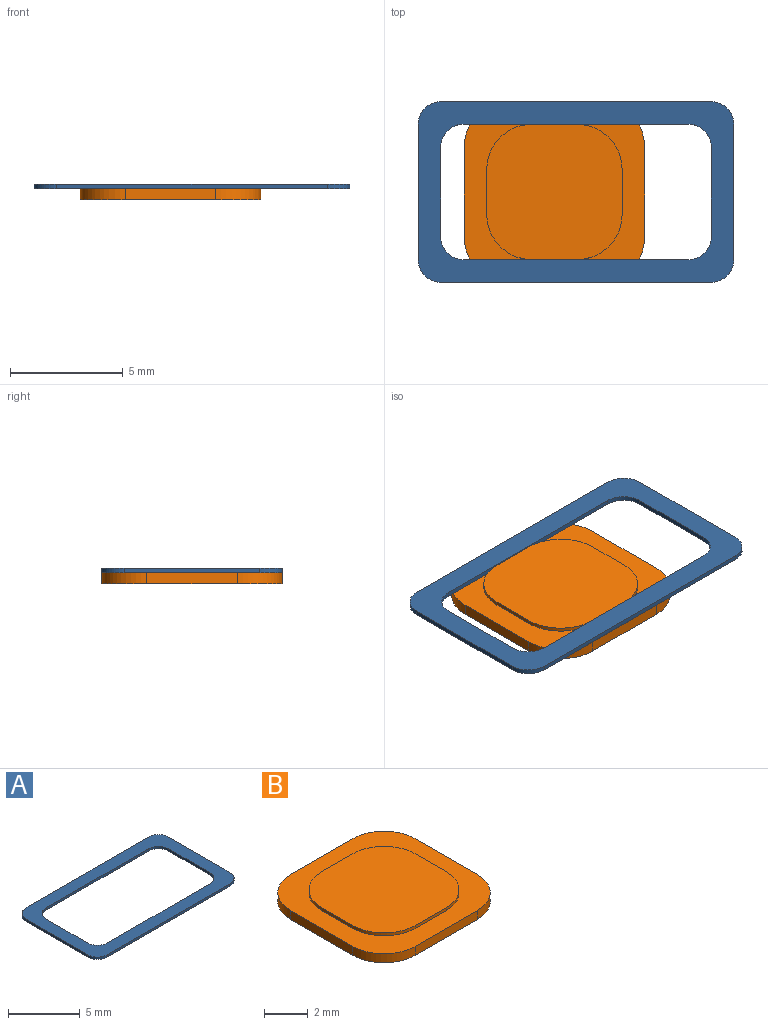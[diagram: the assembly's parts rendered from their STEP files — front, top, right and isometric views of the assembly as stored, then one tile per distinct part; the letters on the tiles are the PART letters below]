
ASSEMBLY  parts=2 mates=1
PART A: 18 faces, bbox 14x8x0.2 mm
  f0: plane 14x8mm, normal (0,0,1), area 40mm2, adj f2,f3,f4,f5,f6,f7,f8,f9
  f1: plane 14x8mm, normal (0,0,-1), area 40mm2, adj f2,f3,f4,f5,f6,f7,f8,f9
  f2: plane 12x0.2mm, normal (0,-1,0), area 2.4mm2, adj f0,f1,f3,f9
  f3: cylinder r=1mm len=1mm, axis (0,0,-1), area 0.3mm2, adj f0,f1,f2,f4
  f4: plane 6x0.2mm, normal (1,0,0), area 1.2mm2, adj f0,f1,f3,f5
  f5: cylinder r=1mm len=1mm, axis (0,0,-1), area 0.3mm2, adj f0,f1,f4,f6
  f6: plane 12x0.2mm, normal (0,1,0), area 2.4mm2, adj f0,f1,f5,f7
  f7: cylinder r=1mm len=1mm, axis (0,0,-1), area 0.3mm2, adj f0,f1,f6,f8
  f8: plane 6x0.2mm, normal (-1,0,0), area 1.2mm2, adj f0,f1,f7,f9
  f9: cylinder r=1mm len=1mm, axis (0,0,-1), area 0.3mm2, adj f0,f1,f2,f8
  f10: cylinder r=1mm len=1mm, axis (0,0,-1), area 0.3mm2, adj f0,f1,f11,f17
  f11: plane 10x0.2mm, normal (0,1,0), area 2mm2, adj f0,f1,f10,f12
  f12: cylinder r=1mm len=1mm, axis (0,0,-1), area 0.3mm2, adj f0,f1,f11,f13
  f13: plane 4x0.2mm, normal (-1,0,0), area 0.8mm2, adj f0,f1,f12,f14
  f14: cylinder r=1mm len=1mm, axis (0,0,-1), area 0.3mm2, adj f0,f1,f13,f15
  f15: plane 10x0.2mm, normal (0,-1,0), area 2mm2, adj f0,f1,f14,f16
  f16: cylinder r=1mm len=1mm, axis (0,0,-1), area 0.3mm2, adj f0,f1,f15,f17
  f17: plane 4x0.2mm, normal (1,0,0), area 0.8mm2, adj f0,f1,f10,f16
PART B: 19 faces, bbox 8x8x0.7 mm
  f0: plane 8x8mm, normal (0,0,1), area 28mm2, adj f1,f2,f3,f4,f5,f6,f7,f8
  f1: cylinder r=2mm len=2mm, axis (0,0,1), area 1.6mm2, adj f0,f2,f8,f9
  f2: plane 4x0.5mm, normal (0,-1,0), area 2mm2, adj f0,f1,f3,f9
  f3: cylinder r=2mm len=2mm, axis (0,0,1), area 1.6mm2, adj f0,f2,f4,f9
  f4: plane 4x0.5mm, normal (1,0,0), area 2mm2, adj f0,f3,f5,f9
  f5: cylinder r=2mm len=2mm, axis (0,0,1), area 1.6mm2, adj f0,f4,f6,f9
  f6: plane 4x0.5mm, normal (0,1,0), area 2mm2, adj f0,f5,f7,f9
  f7: cylinder r=2mm len=2mm, axis (0,0,1), area 1.6mm2, adj f0,f6,f8,f9
  f8: plane 4x0.5mm, normal (-1,0,0), area 2mm2, adj f0,f1,f7,f9
  f9: plane 8x8mm, normal (0,0,-1), area 60.6mm2, adj f1,f2,f3,f4,f5,f6,f7,f8
  f10: plane 2x0.16mm, normal (0,-1,0), area 0.3mm2, adj f0,f11,f17,f18
  f11: cylinder r=2mm len=2mm, axis (0,0,-1), area 0.5mm2, adj f0,f10,f12,f18
  f12: plane 2x0.16mm, normal (1,0,0), area 0.3mm2, adj f0,f11,f13,f18
  f13: cylinder r=2mm len=2mm, axis (0,0,-1), area 0.5mm2, adj f0,f12,f14,f18
  f14: plane 2x0.16mm, normal (0,1,0), area 0.3mm2, adj f0,f13,f15,f18
  f15: cylinder r=2mm len=2mm, axis (0,0,-1), area 0.5mm2, adj f0,f14,f16,f18
  f16: plane 2x0.16mm, normal (-1,0,0), area 0.3mm2, adj f0,f15,f17,f18
  f17: cylinder r=2mm len=2mm, axis (0,0,-1), area 0.5mm2, adj f0,f10,f16,f18
  f18: plane 6x6mm, normal (0,0,1), area 32.6mm2, adj f10,f11,f12,f13,f14,f15,f16,f17
PLACE A rot(axis=(-1,0,0.04),0deg) t=(3.66,0.23,8.26)mm
PLACE B rot(axis=(-1,0,0.04),0deg) t=(2.71,0.23,8.26)mm
MATE slider B.f12 <-> A.f13  axis (1,0,0) through (5.71,0.23,8.34)mm
